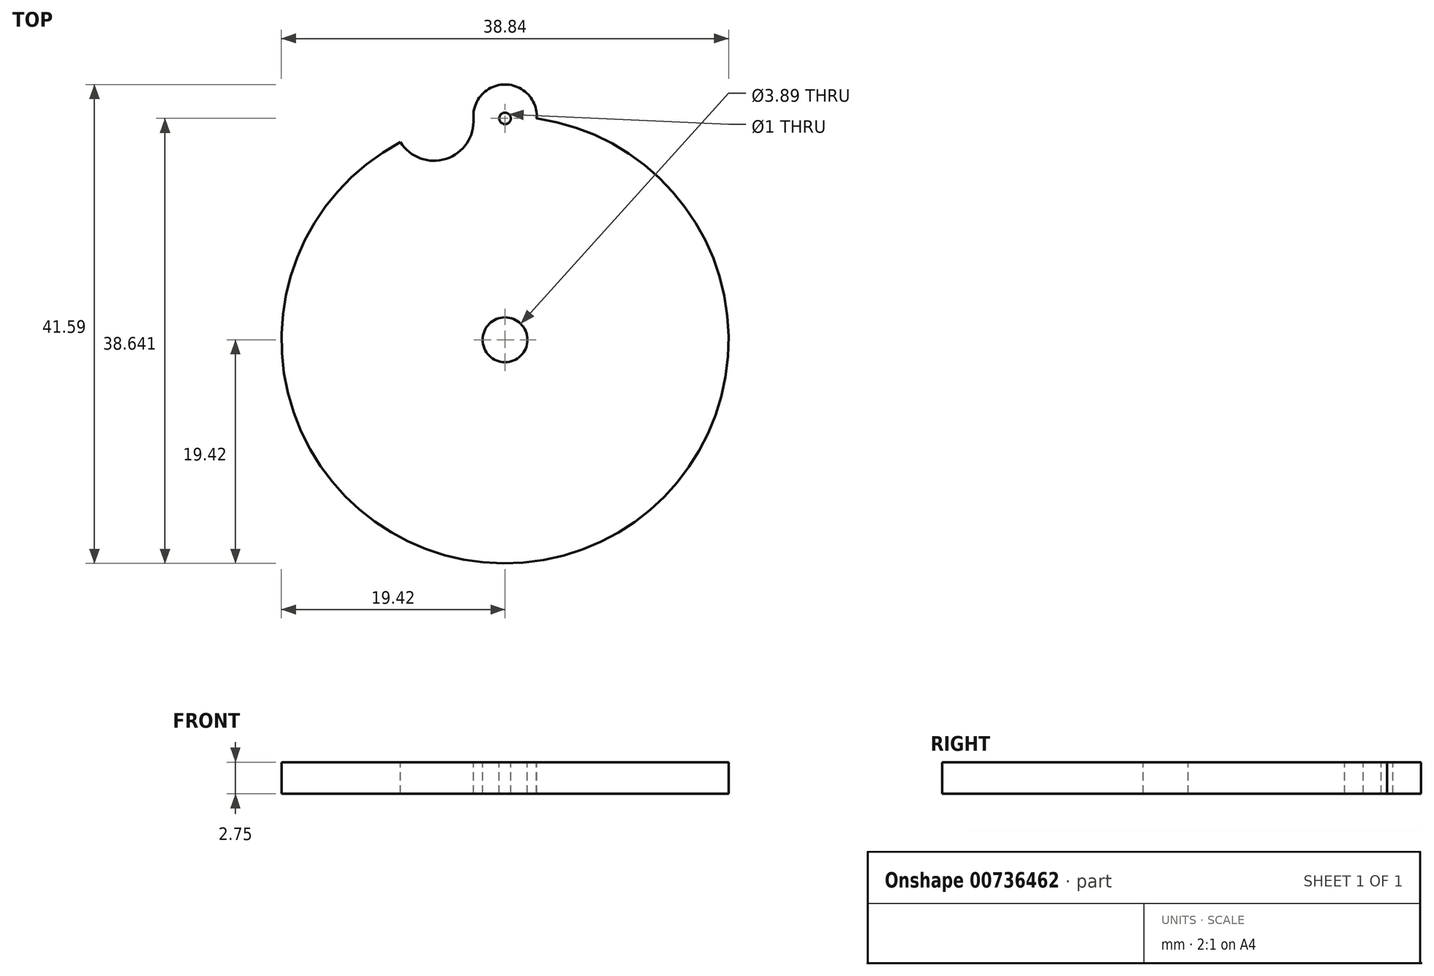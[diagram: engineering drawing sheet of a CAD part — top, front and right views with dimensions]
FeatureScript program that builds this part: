
annotation { "Feature Type Name" : "Feature", "Feature Type Description" : "" }
export const myFeature = defineFeature(function(context is Context, id is Id, definition is map)
    precondition{}
    {
        {
            var Q0;
            Q0=qCreatedBy(makeId("Top.planeOp"),FACE);
            var sketch = newSketch(context, id + "F0", { "sketchPlane" : qUnion([Q0])});
            skCircle(sketch, "E0.cCircle", {"center": v(0, 0) * mm, "radius": 19.42 * mm});
            skSolve(sketch);
        }
        {
            var Q0;
            Q0=makeQuery(id+"F0.imprint","IMPRINT",FACE,{"disambiguationData":[TD([[makeQuery(id+"F0.imprint","IMPRINT",EDGE,{"derivedFrom":sQuery(id+"F0.wireOp",EDGE,"E0.cCircle")}),1.0]])]});
            extrude(context, id + "F1", {"entities" : qUnion([Q0]), "oppositeDirection" : true, "depth" : 2.75 * mm, "offsetDistance" : 25 * mm});
        }
        {
            var Q0;
            Q0=makeQuery(id+"F1.opExtrude","CAP_FACE",FACE,{"disambiguationData":[OSD([sQuery(id+"F0.wireOp",EDGE,"E0.cCircle")])],"isStart":true});
            var sketch = newSketch(context, id + "F2", { "sketchPlane" : qUnion([Q0])});
            skCircle(sketch, "E1.cCircle", {"center": v(0, 0) * mm, "radius": 19.42 * mm, "construction": true});
            skLineSegment(sketch, "E1.0", {"start": v(6, 18.47) * mm, "end": v(15.7, 11.41) * mm, "construction": true});
            skLineSegment(sketch, "E1.1", {"start": v(15.7, 11.41) * mm, "end": v(19.42, 0) * mm, "construction": true});
            skLineSegment(sketch, "E1.2", {"start": v(19.42, 0) * mm, "end": v(15.7, -11.41) * mm, "construction": true});
            skLineSegment(sketch, "E1.3", {"start": v(15.7, -11.41) * mm, "end": v(6, -18.47) * mm, "construction": true});
            skLineSegment(sketch, "E1.4", {"start": v(6, -18.47) * mm, "end": v(-6, -18.47) * mm, "construction": true});
            skLineSegment(sketch, "E1.5", {"start": v(-6, -18.47) * mm, "end": v(-15.7, -11.41) * mm, "construction": true});
            skLineSegment(sketch, "E1.6", {"start": v(-15.7, -11.41) * mm, "end": v(-19.42, 0) * mm, "construction": true});
            skLineSegment(sketch, "E1.7", {"start": v(-19.42, 0) * mm, "end": v(-15.7, 11.41) * mm, "construction": true});
            skLineSegment(sketch, "E1.8", {"start": v(-15.7, 11.41) * mm, "end": v(-6, 18.47) * mm, "construction": true});
            skLineSegment(sketch, "E1.9", {"start": v(-6, 18.47) * mm, "end": v(6, 18.47) * mm, "construction": true});
            skLineSegment(sketch, "E2.0", {"start": v(0, 19.42) * mm, "end": v(11.41, 15.7) * mm, "construction": true});
            skLineSegment(sketch, "E2.1", {"start": v(11.41, 15.7) * mm, "end": v(18.47, 6) * mm, "construction": true});
            skLineSegment(sketch, "E2.2", {"start": v(18.47, 6) * mm, "end": v(18.47, -6) * mm, "construction": true});
            skLineSegment(sketch, "E2.3", {"start": v(18.47, -6) * mm, "end": v(11.41, -15.7) * mm, "construction": true});
            skLineSegment(sketch, "E2.4", {"start": v(11.41, -15.7) * mm, "end": v(0, -19.42) * mm, "construction": true});
            skLineSegment(sketch, "E2.5", {"start": v(0, -19.42) * mm, "end": v(-11.41, -15.7) * mm, "construction": true});
            skLineSegment(sketch, "E2.6", {"start": v(-11.41, -15.7) * mm, "end": v(-18.47, -6) * mm, "construction": true});
            skLineSegment(sketch, "E2.7", {"start": v(-18.47, -6) * mm, "end": v(-18.47, 6) * mm, "construction": true});
            skLineSegment(sketch, "E2.8", {"start": v(-18.47, 6) * mm, "end": v(-11.41, 15.7) * mm, "construction": true});
            skLineSegment(sketch, "E2.9", {"start": v(-11.41, 15.7) * mm, "end": v(0, 19.42) * mm, "construction": true});
            skArc(sketch, "E3", {"start": v(2.74, 19.22) * mm, "mid": v(0, 22.17) * mm, "end": v(-2.74, 19.22) * mm});
            skSolve(sketch);
        }
        {
            var Q0;
            {var subQ0=sQuery(id+"F2.wireOp",EDGE,"E3");Q0=makeQuery(id+"F2.imprint","IMPRINT",FACE,{"disambiguationData":[TD([[makeQuery(id+"F2.imprint","IMPRINT",EDGE,{"derivedFrom":subQ0}),1.0]])]});}
            extrude(context, id + "F3", {"entities" : qUnion([Q0]), "operationType" : NewBodyOperationType.ADD, "oppositeDirection" : true, "depth" : 2.75 * mm, "offsetDistance" : 25 * mm});
        }
        {
            var Q0;
            {var subQ0=sQuery(id+"F2.wireOp",EDGE,"baf49831-05c4-46a7-9bc9-c9a5eefe7398");var subQ1=sQuery(id+"F0.wireOp",EDGE,"E0.cCircle");Q0=makeQuery(id+"FI6q3IJ0qic127d_1.9.F3.boolean.opBoolean","MERGE",FACE,{"derivedFrom":[makeQuery(id+"FI6q3IJ0qic127d_1.8.F3.boolean.opBoolean","MERGE",FACE,{"derivedFrom":[makeQuery(id+"FI6q3IJ0qic127d_1.7.F3.boolean.opBoolean","MERGE",FACE,{"derivedFrom":[makeQuery(id+"FI6q3IJ0qic127d_1.6.F3.boolean.opBoolean","MERGE",FACE,{"derivedFrom":[makeQuery(id+"FI6q3IJ0qic127d_1.5.F3.boolean.opBoolean","MERGE",FACE,{"derivedFrom":[makeQuery(id+"FI6q3IJ0qic127d_1.4.F3.boolean.opBoolean","MERGE",FACE,{"derivedFrom":[makeQuery(id+"FI6q3IJ0qic127d_1.3.F3.boolean.opBoolean","MERGE",FACE,{"derivedFrom":[makeQuery(id+"FI6q3IJ0qic127d_1.2.F3.boolean.opBoolean","MERGE",FACE,{"derivedFrom":[makeQuery(id+"FI6q3IJ0qic127d_1.1.F3.boolean.opBoolean","MERGE",FACE,{"derivedFrom":[makeQuery(id+"F3.boolean.opBoolean","MERGE",FACE,{"derivedFrom":[makeQuery(id+"F1.opExtrude","CAP_FACE",FACE,{"disambiguationData":[OSD([subQ1])],"isStart":true}),makeQuery(id+"F3.opExtrude","CAP_FACE",FACE,{"disambiguationData":[OSD([subQ1,subQ0])],"isStart":true})]}),makeQuery(id+"FI6q3IJ0qic127d_1.1.F3.opExtrude","CAP_FACE",FACE,{"disambiguationData":[OSD([subQ1,subQ0])],"isStart":true})]}),makeQuery(id+"FI6q3IJ0qic127d_1.2.F3.opExtrude","CAP_FACE",FACE,{"disambiguationData":[OSD([subQ1,subQ0])],"isStart":true})]}),makeQuery(id+"FI6q3IJ0qic127d_1.3.F3.opExtrude","CAP_FACE",FACE,{"disambiguationData":[OSD([subQ1,subQ0])],"isStart":true})]}),makeQuery(id+"FI6q3IJ0qic127d_1.4.F3.opExtrude","CAP_FACE",FACE,{"disambiguationData":[OSD([subQ1,subQ0])],"isStart":true})]}),makeQuery(id+"FI6q3IJ0qic127d_1.5.F3.opExtrude","CAP_FACE",FACE,{"disambiguationData":[OSD([subQ1,subQ0])],"isStart":true})]}),makeQuery(id+"FI6q3IJ0qic127d_1.6.F3.opExtrude","CAP_FACE",FACE,{"disambiguationData":[OSD([subQ1,subQ0])],"isStart":true})]}),makeQuery(id+"FI6q3IJ0qic127d_1.7.F3.opExtrude","CAP_FACE",FACE,{"disambiguationData":[OSD([subQ1,subQ0])],"isStart":true})]}),makeQuery(id+"FI6q3IJ0qic127d_1.8.F3.opExtrude","CAP_FACE",FACE,{"disambiguationData":[OSD([subQ1,subQ0])],"isStart":true})]}),makeQuery(id+"FI6q3IJ0qic127d_1.9.F3.opExtrude","CAP_FACE",FACE,{"disambiguationData":[OSD([subQ1,subQ0])],"isStart":true})]});}
            var sketch = newSketch(context, id + "F4", { "sketchPlane" : qUnion([Q0])});
            skLineSegment(sketch, "E4", {"start": v(-9.08, 17.16) * mm, "end": v(-6.24, 19.2) * mm});
            skLineSegment(sketch, "E5", {"start": v(-6.24, 19.2) * mm, "end": v(-2.74, 19.22) * mm});
            skArc(sketch, "E6", {"start": v(-9.08, 17.16) * mm, "mid": v(-5.1, 15.71) * mm, "end": v(-2.74, 19.22) * mm});
            skSolve(sketch);
        }
        {
            var Q0;
            Q0 = qSketchRegion(id + "F4", true);
            extrude(context, id + "F5", {"entities" : qUnion([Q0]), "operationType" : NewBodyOperationType.REMOVE, "oppositeDirection" : true, "depth" : 25 * mm, "offsetDistance" : 25 * mm});
        }
        {
            var Q0;
            {var subQ0=sQuery(id+"F2.wireOp",EDGE,"baf49831-05c4-46a7-9bc9-c9a5eefe7398");var subQ1=sQuery(id+"F0.wireOp",EDGE,"E0.cCircle");Q0=makeQuery(id+"FI6q3IJ0qic127d_1.9.F3.boolean.opBoolean","MERGE",FACE,{"derivedFrom":[makeQuery(id+"FI6q3IJ0qic127d_1.8.F3.boolean.opBoolean","MERGE",FACE,{"derivedFrom":[makeQuery(id+"FI6q3IJ0qic127d_1.7.F3.boolean.opBoolean","MERGE",FACE,{"derivedFrom":[makeQuery(id+"FI6q3IJ0qic127d_1.6.F3.boolean.opBoolean","MERGE",FACE,{"derivedFrom":[makeQuery(id+"FI6q3IJ0qic127d_1.5.F3.boolean.opBoolean","MERGE",FACE,{"derivedFrom":[makeQuery(id+"FI6q3IJ0qic127d_1.4.F3.boolean.opBoolean","MERGE",FACE,{"derivedFrom":[makeQuery(id+"FI6q3IJ0qic127d_1.3.F3.boolean.opBoolean","MERGE",FACE,{"derivedFrom":[makeQuery(id+"FI6q3IJ0qic127d_1.2.F3.boolean.opBoolean","MERGE",FACE,{"derivedFrom":[makeQuery(id+"FI6q3IJ0qic127d_1.1.F3.boolean.opBoolean","MERGE",FACE,{"derivedFrom":[makeQuery(id+"F3.boolean.opBoolean","MERGE",FACE,{"derivedFrom":[makeQuery(id+"F1.opExtrude","CAP_FACE",FACE,{"disambiguationData":[OSD([subQ1])],"isStart":true}),makeQuery(id+"F3.opExtrude","CAP_FACE",FACE,{"disambiguationData":[OSD([subQ1,subQ0])],"isStart":true})]}),makeQuery(id+"FI6q3IJ0qic127d_1.1.F3.opExtrude","CAP_FACE",FACE,{"disambiguationData":[OSD([subQ1,subQ0])],"isStart":true})]}),makeQuery(id+"FI6q3IJ0qic127d_1.2.F3.opExtrude","CAP_FACE",FACE,{"disambiguationData":[OSD([subQ1,subQ0])],"isStart":true})]}),makeQuery(id+"FI6q3IJ0qic127d_1.3.F3.opExtrude","CAP_FACE",FACE,{"disambiguationData":[OSD([subQ1,subQ0])],"isStart":true})]}),makeQuery(id+"FI6q3IJ0qic127d_1.4.F3.opExtrude","CAP_FACE",FACE,{"disambiguationData":[OSD([subQ1,subQ0])],"isStart":true})]}),makeQuery(id+"FI6q3IJ0qic127d_1.5.F3.opExtrude","CAP_FACE",FACE,{"disambiguationData":[OSD([subQ1,subQ0])],"isStart":true})]}),makeQuery(id+"FI6q3IJ0qic127d_1.6.F3.opExtrude","CAP_FACE",FACE,{"disambiguationData":[OSD([subQ1,subQ0])],"isStart":true})]}),makeQuery(id+"FI6q3IJ0qic127d_1.7.F3.opExtrude","CAP_FACE",FACE,{"disambiguationData":[OSD([subQ1,subQ0])],"isStart":true})]}),makeQuery(id+"FI6q3IJ0qic127d_1.8.F3.opExtrude","CAP_FACE",FACE,{"disambiguationData":[OSD([subQ1,subQ0])],"isStart":true})]}),makeQuery(id+"FI6q3IJ0qic127d_1.9.F3.opExtrude","CAP_FACE",FACE,{"disambiguationData":[OSD([subQ1,subQ0])],"isStart":true})]});}
            var sketch = newSketch(context, id + "F6", { "sketchPlane" : qUnion([Q0])});
            skCircle(sketch, "E7", {"center": v(0, 0) * mm, "radius": 1.95 * mm});
            skSolve(sketch);
        }
        {
            var Q0;
            Q0 = qSketchRegion(id + "F6", true);
            extrude(context, id + "F7", {"entities" : qUnion([Q0]), "operationType" : NewBodyOperationType.REMOVE, "oppositeDirection" : true, "depth" : 25 * mm, "offsetDistance" : 25 * mm});
        }
        {
            var Q0;
            {var subQ0=sQuery(id+"F2.wireOp",EDGE,"baf49831-05c4-46a7-9bc9-c9a5eefe7398");var subQ1=sQuery(id+"F0.wireOp",EDGE,"E0.cCircle");Q0=makeQuery(id+"FI6q3IJ0qic127d_1.9.F3.boolean.opBoolean","MERGE",FACE,{"derivedFrom":[makeQuery(id+"FI6q3IJ0qic127d_1.8.F3.boolean.opBoolean","MERGE",FACE,{"derivedFrom":[makeQuery(id+"FI6q3IJ0qic127d_1.7.F3.boolean.opBoolean","MERGE",FACE,{"derivedFrom":[makeQuery(id+"FI6q3IJ0qic127d_1.6.F3.boolean.opBoolean","MERGE",FACE,{"derivedFrom":[makeQuery(id+"FI6q3IJ0qic127d_1.5.F3.boolean.opBoolean","MERGE",FACE,{"derivedFrom":[makeQuery(id+"FI6q3IJ0qic127d_1.4.F3.boolean.opBoolean","MERGE",FACE,{"derivedFrom":[makeQuery(id+"FI6q3IJ0qic127d_1.3.F3.boolean.opBoolean","MERGE",FACE,{"derivedFrom":[makeQuery(id+"FI6q3IJ0qic127d_1.2.F3.boolean.opBoolean","MERGE",FACE,{"derivedFrom":[makeQuery(id+"FI6q3IJ0qic127d_1.1.F3.boolean.opBoolean","MERGE",FACE,{"derivedFrom":[makeQuery(id+"F3.boolean.opBoolean","MERGE",FACE,{"derivedFrom":[makeQuery(id+"F1.opExtrude","CAP_FACE",FACE,{"disambiguationData":[OSD([subQ1])],"isStart":true}),makeQuery(id+"F3.opExtrude","CAP_FACE",FACE,{"disambiguationData":[OSD([subQ1,subQ0])],"isStart":true})]}),makeQuery(id+"FI6q3IJ0qic127d_1.1.F3.opExtrude","CAP_FACE",FACE,{"disambiguationData":[OSD([subQ1,subQ0])],"isStart":true})]}),makeQuery(id+"FI6q3IJ0qic127d_1.2.F3.opExtrude","CAP_FACE",FACE,{"disambiguationData":[OSD([subQ1,subQ0])],"isStart":true})]}),makeQuery(id+"FI6q3IJ0qic127d_1.3.F3.opExtrude","CAP_FACE",FACE,{"disambiguationData":[OSD([subQ1,subQ0])],"isStart":true})]}),makeQuery(id+"FI6q3IJ0qic127d_1.4.F3.opExtrude","CAP_FACE",FACE,{"disambiguationData":[OSD([subQ1,subQ0])],"isStart":true})]}),makeQuery(id+"FI6q3IJ0qic127d_1.5.F3.opExtrude","CAP_FACE",FACE,{"disambiguationData":[OSD([subQ1,subQ0])],"isStart":true})]}),makeQuery(id+"FI6q3IJ0qic127d_1.6.F3.opExtrude","CAP_FACE",FACE,{"disambiguationData":[OSD([subQ1,subQ0])],"isStart":true})]}),makeQuery(id+"FI6q3IJ0qic127d_1.7.F3.opExtrude","CAP_FACE",FACE,{"disambiguationData":[OSD([subQ1,subQ0])],"isStart":true})]}),makeQuery(id+"FI6q3IJ0qic127d_1.8.F3.opExtrude","CAP_FACE",FACE,{"disambiguationData":[OSD([subQ1,subQ0])],"isStart":true})]}),makeQuery(id+"FI6q3IJ0qic127d_1.9.F3.opExtrude","CAP_FACE",FACE,{"disambiguationData":[OSD([subQ1,subQ0])],"isStart":true})]});}
            var sketch = newSketch(context, id + "F8", { "sketchPlane" : qUnion([Q0])});
            skCircle(sketch, "E8", {"center": v(0, 19.22) * mm, "radius": 0.5 * mm});
            skSolve(sketch);
        }
        {
            var Q0;
            Q0 = qSketchRegion(id + "F8", true);
            extrude(context, id + "F9", {"entities" : qUnion([Q0]), "operationType" : NewBodyOperationType.REMOVE, "oppositeDirection" : true, "depth" : 25 * mm, "offsetDistance" : 25 * mm});
        }
    });
